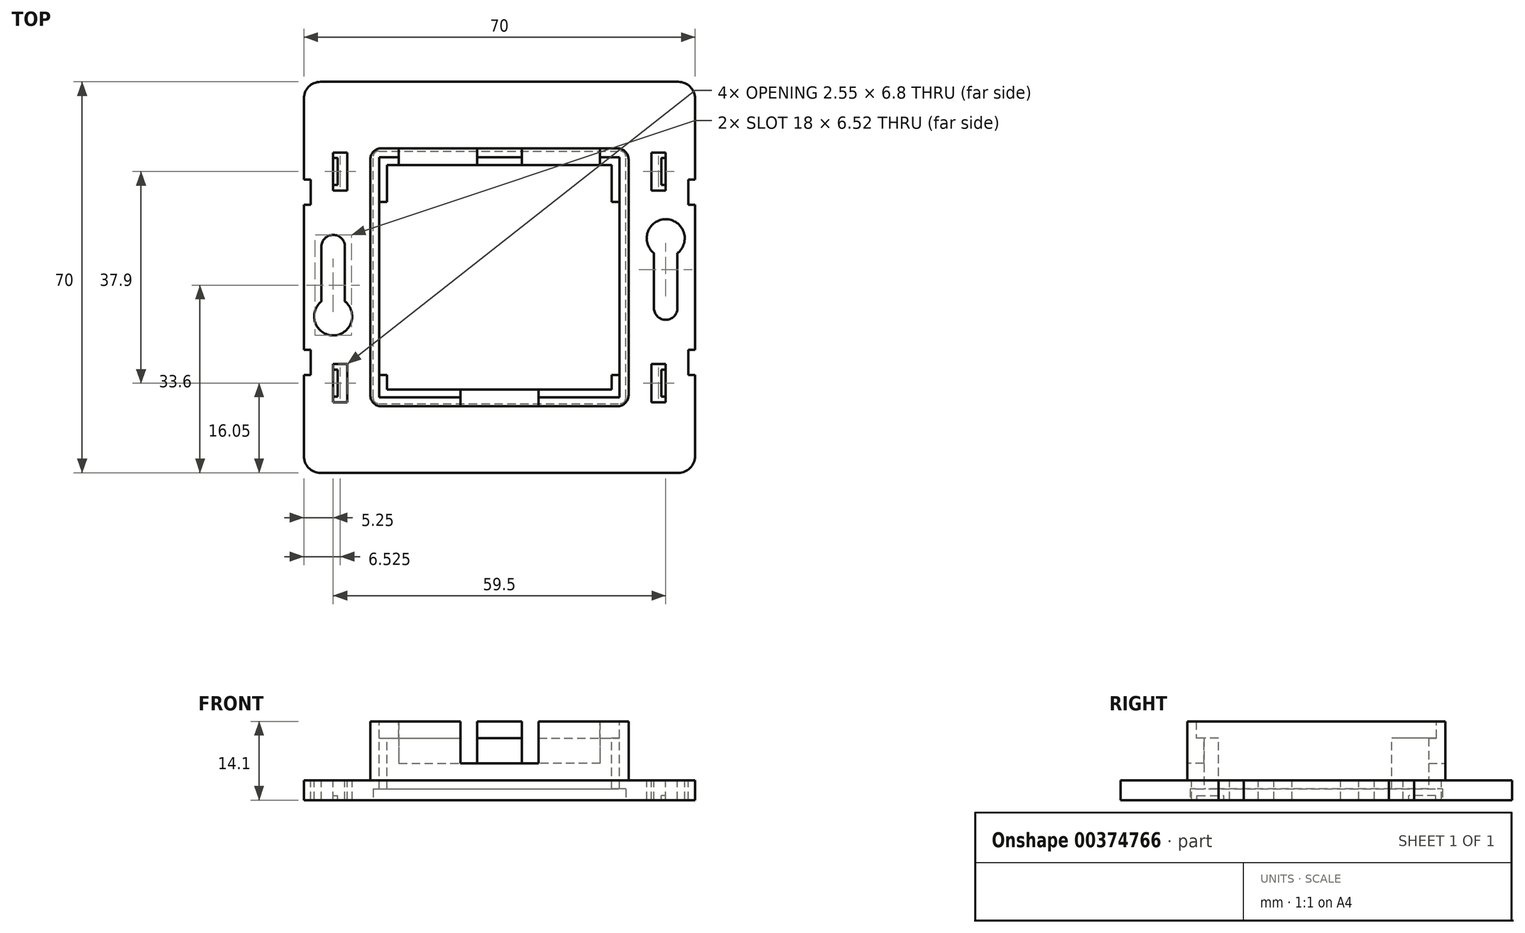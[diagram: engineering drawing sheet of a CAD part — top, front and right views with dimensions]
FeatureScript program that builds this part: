
annotation { "Feature Type Name" : "Feature", "Feature Type Description" : "" }
export const myFeature = defineFeature(function(context is Context, id is Id, definition is map)
    precondition{}
    {
        {
            var Q0;
            Q0=qCreatedBy(makeId("Top.planeOp"),FACE);
            var sketch = newSketch(context, id + "F0", { "sketchPlane" : qUnion([Q0])});
            skLineSegment(sketch, "E0.bottom", {"start": v(-32, 35) * mm, "end": v(32, 35) * mm});
            skLineSegment(sketch, "E0.top", {"start": v(-32, -35) * mm, "end": v(32, -35) * mm});
            skLineSegment(sketch, "E0.left", {"start": v(-35, 32) * mm, "end": v(-35, -32) * mm});
            skLineSegment(sketch, "E0.right", {"start": v(35, 32) * mm, "end": v(35, -32) * mm});
            skPoint(sketch, "E1.visualSharp", {"position": v(-35, 35) * mm});
            skArc(sketch, "E1.filletArc", {"start": v(-32, 35) * mm, "mid": v(-34.12, 34.12) * mm, "end": v(-35, 32) * mm});
            skPoint(sketch, "E2.visualSharp", {"position": v(35, 35) * mm});
            skArc(sketch, "E2.filletArc", {"start": v(35, 32) * mm, "mid": v(34.12, 34.12) * mm, "end": v(32, 35) * mm});
            skPoint(sketch, "E3.visualSharp", {"position": v(35, -35) * mm});
            skArc(sketch, "E3.filletArc", {"start": v(32, -35) * mm, "mid": v(34.12, -34.12) * mm, "end": v(35, -32) * mm});
            skPoint(sketch, "E4.visualSharp", {"position": v(-35, -35) * mm});
            skArc(sketch, "E4.filletArc", {"start": v(-35, -32) * mm, "mid": v(-34.12, -34.12) * mm, "end": v(-32, -35) * mm});
            skLineSegment(sketch, "E5.bottom", {"start": v(-20.1, 20.1) * mm, "end": v(20.1, 20.1) * mm});
            skLineSegment(sketch, "E5.top", {"start": v(-20.1, -20.1) * mm, "end": v(20.1, -20.1) * mm});
            skLineSegment(sketch, "E5.left", {"start": v(-20.1, 20.1) * mm, "end": v(-20.1, -20.1) * mm});
            skLineSegment(sketch, "E5.right", {"start": v(20.1, 20.1) * mm, "end": v(20.1, -20.1) * mm});
            skLineSegment(sketch, "E6.0", {"start": v(23.1, 21.1) * mm, "end": v(23.1, -21.1) * mm});
            skLineSegment(sketch, "E6.1", {"start": v(-21.1, 23.1) * mm, "end": v(21.1, 23.1) * mm});
            skLineSegment(sketch, "E6.2", {"start": v(-23.1, 21.1) * mm, "end": v(-23.1, -21.1) * mm});
            skLineSegment(sketch, "E6.3", {"start": v(-21.1, -23.1) * mm, "end": v(21.1, -23.1) * mm});
            skPoint(sketch, "E7.visualSharp", {"position": v(-23.1, 23.1) * mm});
            skArc(sketch, "E7.filletArc", {"start": v(-21.1, 23.1) * mm, "mid": v(-22.51, 22.51) * mm, "end": v(-23.1, 21.1) * mm});
            skPoint(sketch, "E8.visualSharp", {"position": v(23.1, 23.1) * mm});
            skArc(sketch, "E8.filletArc", {"start": v(23.1, 21.1) * mm, "mid": v(22.51, 22.51) * mm, "end": v(21.1, 23.1) * mm});
            skPoint(sketch, "E9.visualSharp", {"position": v(23.1, -23.1) * mm});
            skArc(sketch, "E9.filletArc", {"start": v(21.1, -23.1) * mm, "mid": v(22.51, -22.51) * mm, "end": v(23.1, -21.1) * mm});
            skPoint(sketch, "E10.visualSharp", {"position": v(-23.1, -23.1) * mm});
            skArc(sketch, "E10.filletArc", {"start": v(-23.1, -21.1) * mm, "mid": v(-22.51, -22.51) * mm, "end": v(-21.1, -23.1) * mm});
            skSolve(sketch);
        }
        {
            var Q0;
            Q0=makeQuery(id+"F0.imprint","IMPRINT",FACE,{"disambiguationData":[TD([[makeQuery(id+"F0.imprint","IMPRINT",EDGE,{"derivedFrom":sQuery(id+"F0.wireOp",EDGE,"E5.bottom")}),1.0]])]});
            extrude(context, id + "F1", {"entities" : qUnion([Q0]), "depth" : 14.1 * mm});
        }
        {
            var Q0;
            Q0=makeQuery(id+"F0.imprint","IMPRINT",FACE,{"disambiguationData":[TD([[makeQuery(id+"F0.imprint","IMPRINT",EDGE,{"derivedFrom":sQuery(id+"F0.wireOp",EDGE,"E0.bottom")}),-1.0]])]});
            extrude(context, id + "F2", {"entities" : qUnion([Q0]), "operationType" : NewBodyOperationType.ADD, "depth" : 3.5 * mm});
        }
        {
            var Q0;
            Q0=makeQuery(id+"F2.opExtrude","CAP_FACE",FACE,{"disambiguationData":[OSD([sQuery(id+"F0.wireOp",EDGE,"E0.bottom"),sQuery(id+"F0.wireOp",EDGE,"E0.top"),sQuery(id+"F0.wireOp",EDGE,"E0.left"),sQuery(id+"F0.wireOp",EDGE,"E0.right"),sQuery(id+"F0.wireOp",EDGE,"8215a4ff-56be-4c60-a47c-f66ea536b4aa.0"),sQuery(id+"F0.wireOp",EDGE,"8215a4ff-56be-4c60-a47c-f66ea536b4aa.1"),sQuery(id+"F0.wireOp",EDGE,"8215a4ff-56be-4c60-a47c-f66ea536b4aa.2"),sQuery(id+"F0.wireOp",EDGE,"8215a4ff-56be-4c60-a47c-f66ea536b4aa.3"),sQuery(id+"F0.wireOp",EDGE,"E1.filletArc"),sQuery(id+"F0.wireOp",EDGE,"E2.filletArc"),sQuery(id+"F0.wireOp",EDGE,"E3.filletArc"),sQuery(id+"F0.wireOp",EDGE,"E4.filletArc"),sQuery(id+"F0.wireOp",EDGE,"55755b73-03b5-497c-a17b-18f3f700d980.filletArc"),sQuery(id+"F0.wireOp",EDGE,"18d8bc87-035d-4be4-8c5c-5c0431c61aee.filletArc"),sQuery(id+"F0.wireOp",EDGE,"c21042aa-8350-4172-84ff-4aa2e3af1f04.filletArc"),sQuery(id+"F0.wireOp",EDGE,"eb6bf6a7-3b97-4e9c-9c9c-5d018f2c8f51.filletArc")])],"isStart":false});
            var sketch = newSketch(context, id + "F3", { "sketchPlane" : qUnion([Q0])});
            skLineSegment(sketch, "E11.bottom", {"start": v(-35, 13) * mm, "end": v(-33.8, 13) * mm});
            skLineSegment(sketch, "E11.top", {"start": v(-35, 17.5) * mm, "end": v(-33.8, 17.5) * mm});
            skLineSegment(sketch, "E11.left", {"start": v(-35, 17.5) * mm, "end": v(-35, 13) * mm});
            skLineSegment(sketch, "E11.right", {"start": v(-33.8, 17.5) * mm, "end": v(-33.8, 13) * mm});
            skLineSegment(sketch, "E12.bottom", {"start": v(35, -17.5) * mm, "end": v(33.8, -17.5) * mm});
            skLineSegment(sketch, "E12.top", {"start": v(35, -13) * mm, "end": v(33.8, -13) * mm});
            skLineSegment(sketch, "E12.left", {"start": v(35, -17.5) * mm, "end": v(35, -13) * mm});
            skLineSegment(sketch, "E12.right", {"start": v(33.8, -17.5) * mm, "end": v(33.8, -13) * mm});
            skArc(sketch, "E13", {"start": v(31.85, 4.33) * mm, "mid": v(29.75, 10.4) * mm, "end": v(27.65, 4.33) * mm});
            skArc(sketch, "E14", {"start": v(27.65, -5.5) * mm, "mid": v(29.75, -7.6) * mm, "end": v(31.85, -5.5) * mm});
            skLineSegment(sketch, "E15", {"start": v(27.65, -5.5) * mm, "end": v(27.65, 4.33) * mm});
            skLineSegment(sketch, "E16", {"start": v(31.85, -5.5) * mm, "end": v(31.85, 4.33) * mm});
            skArc(sketch, "E17.MirrorC", {"start": v(-31.85, 5.5) * mm, "mid": v(-29.75, 7.6) * mm, "end": v(-27.65, 5.5) * mm});
            skLineSegment(sketch, "E18.MirrorCS", {"start": v(-27.65, 5.5) * mm, "end": v(-27.65, -4.33) * mm});
            skLineSegment(sketch, "E19.MirrorCS", {"start": v(-31.85, 5.5) * mm, "end": v(-31.85, -4.33) * mm});
            skArc(sketch, "E20.MirrorC", {"start": v(-27.65, -4.33) * mm, "mid": v(-29.75, -10.4) * mm, "end": v(-31.85, -4.33) * mm});
            skLineSegment(sketch, "E21.MirrorCS", {"start": v(33.8, 17.5) * mm, "end": v(33.8, 13) * mm});
            skLineSegment(sketch, "E22.MirrorCS", {"start": v(35, 17.5) * mm, "end": v(35, 13) * mm});
            skLineSegment(sketch, "E23.MirrorCS", {"start": v(35, 17.5) * mm, "end": v(33.8, 17.5) * mm});
            skLineSegment(sketch, "E24.MirrorCS", {"start": v(35, 13) * mm, "end": v(33.8, 13) * mm});
            skLineSegment(sketch, "E25.MirrorCS", {"start": v(-35, -17.5) * mm, "end": v(-35, -13) * mm});
            skLineSegment(sketch, "E26.MirrorCS", {"start": v(-33.8, -17.5) * mm, "end": v(-33.8, -13) * mm});
            skLineSegment(sketch, "E27.MirrorCS", {"start": v(-35, -13) * mm, "end": v(-33.8, -13) * mm});
            skLineSegment(sketch, "E28.MirrorCS", {"start": v(-35, -17.5) * mm, "end": v(-33.8, -17.5) * mm});
            skSolve(sketch);
        }
        {
            var Q0;
            Q0 = qSketchRegion(id + "F3", true);
            extrude(context, id + "F4", {"entities" : qUnion([Q0]), "operationType" : NewBodyOperationType.REMOVE, "oppositeDirection" : true, "depth" : 25 * mm});
        }
        {
            var Q0;
            Q0=qCreatedBy(makeId("Top.planeOp"),FACE);
            var sketch = newSketch(context, id + "F5", { "sketchPlane" : qUnion([Q0])});
            skLineSegment(sketch, "E29.bottom", {"start": v(-21.6, -22.6) * mm, "end": v(21.6, -22.6) * mm});
            skLineSegment(sketch, "E29.top", {"start": v(-21.6, 22.6) * mm, "end": v(21.6, 22.6) * mm});
            skLineSegment(sketch, "E29.left", {"start": v(-22.6, -21.6) * mm, "end": v(-22.6, 21.6) * mm});
            skLineSegment(sketch, "E29.right", {"start": v(22.6, -21.6) * mm, "end": v(22.6, 21.6) * mm});
            skPoint(sketch, "E30.visualSharp", {"position": v(-22.6, -22.6) * mm});
            skArc(sketch, "E30.filletArc", {"start": v(-22.6, -21.6) * mm, "mid": v(-22.3, -22.3) * mm, "end": v(-21.6, -22.6) * mm});
            skPoint(sketch, "E31.visualSharp", {"position": v(22.6, -22.6) * mm});
            skArc(sketch, "E31.filletArc", {"start": v(21.6, -22.6) * mm, "mid": v(22.3, -22.3) * mm, "end": v(22.6, -21.6) * mm});
            skPoint(sketch, "E32.visualSharp", {"position": v(22.6, 22.6) * mm});
            skArc(sketch, "E32.filletArc", {"start": v(22.6, 21.6) * mm, "mid": v(22.3, 22.3) * mm, "end": v(21.6, 22.6) * mm});
            skPoint(sketch, "E33.visualSharp", {"position": v(-22.6, 22.6) * mm});
            skArc(sketch, "E33.filletArc", {"start": v(-21.6, 22.6) * mm, "mid": v(-22.3, 22.3) * mm, "end": v(-22.6, 21.6) * mm});
            skSolve(sketch);
        }
        {
            var Q0;
            Q0 = qSketchRegion(id + "F5", true);
            extrude(context, id + "F6", {"entities" : qUnion([Q0]), "operationType" : NewBodyOperationType.REMOVE, "depth" : 2 * mm});
        }
        {
            var Q0;
            Q0=makeQuery(id+"F1.opExtrude","CAP_FACE",FACE,{"disambiguationData":[OSD([sQuery(id+"F0.wireOp",EDGE,"E5.bottom"),sQuery(id+"F0.wireOp",EDGE,"E5.top"),sQuery(id+"F0.wireOp",EDGE,"E5.left"),sQuery(id+"F0.wireOp",EDGE,"E5.right"),sQuery(id+"F0.wireOp",EDGE,"E6.0"),sQuery(id+"F0.wireOp",EDGE,"E6.1"),sQuery(id+"F0.wireOp",EDGE,"E6.2"),sQuery(id+"F0.wireOp",EDGE,"E6.3"),sQuery(id+"F0.wireOp",EDGE,"E7.filletArc"),sQuery(id+"F0.wireOp",EDGE,"E8.filletArc"),sQuery(id+"F0.wireOp",EDGE,"E9.filletArc"),sQuery(id+"F0.wireOp",EDGE,"E10.filletArc")])],"isStart":false});
            var sketch = newSketch(context, id + "F7", { "sketchPlane" : qUnion([Q0])});
            skLineSegment(sketch, "E34.bottom", {"start": v(-20.1, 20.1) * mm, "end": v(20.1, 20.1) * mm});
            skLineSegment(sketch, "E34.top", {"start": v(-20.1, -20.1) * mm, "end": v(20.1, -20.1) * mm});
            skLineSegment(sketch, "E34.left", {"start": v(-20.1, 20.1) * mm, "end": v(-20.1, -20.1) * mm});
            skLineSegment(sketch, "E34.right", {"start": v(20.1, 20.1) * mm, "end": v(20.1, -20.1) * mm});
            skLineSegment(sketch, "E35.0", {"start": v(-21.5, -21.5) * mm, "end": v(21.5, -21.5) * mm});
            skLineSegment(sketch, "E35.1", {"start": v(-21.5, 21.5) * mm, "end": v(-21.5, -21.5) * mm});
            skLineSegment(sketch, "E35.2", {"start": v(-21.5, 21.5) * mm, "end": v(21.5, 21.5) * mm});
            skLineSegment(sketch, "E35.3", {"start": v(21.5, 21.5) * mm, "end": v(21.5, -21.5) * mm});
            skSolve(sketch);
        }
        {
            var Q0;
            Q0=makeQuery(id+"F7.imprint","IMPRINT",FACE,{"disambiguationData":[TD([[makeQuery(id+"F7.imprint","IMPRINT",EDGE,{"derivedFrom":sQuery(id+"F7.wireOp",EDGE,"E34.bottom")}),1.0]])]});
            extrude(context, id + "F8", {"entities" : qUnion([Q0]), "operationType" : NewBodyOperationType.REMOVE, "oppositeDirection" : true, "depth" : 3 * mm});
        }
        {
            var Q0;
            Q0=makeQuery(id+"F1.opExtrude","SWEPT_FACE",FACE,{"disambiguationData":[OSD([sQuery(id+"F0.wireOp",EDGE,"E6.3")])]});
            var sketch = newSketch(context, id + "F9", { "sketchPlane" : qUnion([Q0])});
            skLineSegment(sketch, "E36.bottom", {"start": v(-7, 14.1) * mm, "end": v(7, 14.1) * mm});
            skLineSegment(sketch, "E36.top", {"start": v(-7, 6.6) * mm, "end": v(7, 6.6) * mm});
            skLineSegment(sketch, "E36.left", {"start": v(-7, 14.1) * mm, "end": v(-7, 6.6) * mm});
            skLineSegment(sketch, "E36.right", {"start": v(7, 14.1) * mm, "end": v(7, 6.6) * mm});
            skSolve(sketch);
        }
        {
            var Q0;
            Q0=makeQuery(id+"F9.imprint","IMPRINT",FACE,{"disambiguationData":[TD([[makeQuery(id+"F9.imprint","IMPRINT",EDGE,{"derivedFrom":sQuery(id+"F9.wireOp",EDGE,"E36.bottom")}),-1.0]])]});
            extrude(context, id + "F10", {"entities" : qUnion([Q0]), "operationType" : NewBodyOperationType.REMOVE, "oppositeDirection" : true, "depth" : 5 * mm});
        }
        {
            var Q0;
            Q0=makeQuery(id+"F1.opExtrude","SWEPT_FACE",FACE,{"disambiguationData":[OSD([sQuery(id+"F0.wireOp",EDGE,"E6.1")])]});
            var sketch = newSketch(context, id + "F11", { "sketchPlane" : qUnion([Q0])});
            skLineSegment(sketch, "E37.bottom", {"start": v(-18, 14.1) * mm, "end": v(-4, 14.1) * mm});
            skLineSegment(sketch, "E37.top", {"start": v(-18, 6.6) * mm, "end": v(-4, 6.6) * mm});
            skLineSegment(sketch, "E37.left", {"start": v(-18, 14.1) * mm, "end": v(-18, 6.6) * mm});
            skLineSegment(sketch, "E37.right", {"start": v(-4, 14.1) * mm, "end": v(-4, 6.6) * mm});
            skLineSegment(sketch, "E38.MirrorCS", {"start": v(18, 6.6) * mm, "end": v(4, 6.6) * mm});
            skLineSegment(sketch, "E39.MirrorCS", {"start": v(4, 14.1) * mm, "end": v(4, 6.6) * mm});
            skLineSegment(sketch, "E40.MirrorCS", {"start": v(18, 14.1) * mm, "end": v(18, 6.6) * mm});
            skLineSegment(sketch, "E41.MirrorCS", {"start": v(18, 14.1) * mm, "end": v(4, 14.1) * mm});
            skSolve(sketch);
        }
        {
            var Q0;
            Q0=makeQuery(id+"F11.imprint","IMPRINT",FACE,{"disambiguationData":[TD([[makeQuery(id+"F11.imprint","IMPRINT",EDGE,{"derivedFrom":sQuery(id+"F11.wireOp",EDGE,"E37.bottom")}),1.0]])]});
            var Q1;
            Q1=makeQuery(id+"F11.imprint","IMPRINT",FACE,{"disambiguationData":[TD([[makeQuery(id+"F11.imprint","IMPRINT",EDGE,{"derivedFrom":sQuery(id+"F11.wireOp",EDGE,"E38.MirrorCS")}),-1.0]])]});
            extrude(context, id + "F12", {"entities" : qUnion([Q0, Q1]), "operationType" : NewBodyOperationType.REMOVE, "oppositeDirection" : true, "depth" : 5 * mm});
        }
        {
            var Q0;
            {var subQ0=sQuery(id+"F7.wireOp",EDGE,"E35.2");var subQ1=sQuery(id+"F7.wireOp",EDGE,"E35.1");var subQ2=sQuery(id+"F7.wireOp",EDGE,"E35.0");Q0=makeQuery(id+"F12.boolean.opBoolean","SPLIT",FACE,{"disambiguationData":[TD([makeQuery(id+"F1.opExtrude","SWEPT_FACE",FACE,{"disambiguationData":[OSD([sQuery(id+"F0.wireOp",EDGE,"E5.left")])]})])],"derivedFrom":makeQuery(id+"F8.boolean.opBoolean","COPY",FACE,{"derivedFrom":makeQuery(id+"F8.opExtrude","CAP_FACE",FACE,{"disambiguationData":[OSD([sQuery(id+"F7.wireOp",EDGE,"E34.bottom"),sQuery(id+"F7.wireOp",EDGE,"E34.top"),sQuery(id+"F7.wireOp",EDGE,"E34.left"),sQuery(id+"F7.wireOp",EDGE,"E34.right"),subQ2,subQ1,subQ0,sQuery(id+"F7.wireOp",EDGE,"E35.3")])],"isStart":false})})});}
            var sketch = newSketch(context, id + "F13", { "sketchPlane" : qUnion([Q0])});
            skLineSegment(sketch, "E42.bottom", {"start": v(-21.5, 13.5) * mm, "end": v(-20.1, 13.5) * mm});
            skLineSegment(sketch, "E42.top", {"start": v(-21.5, -17.5) * mm, "end": v(-20.1, -17.5) * mm});
            skLineSegment(sketch, "E42.left", {"start": v(-21.5, 13.5) * mm, "end": v(-21.5, -17.5) * mm});
            skLineSegment(sketch, "E42.right", {"start": v(-20.1, 13.5) * mm, "end": v(-20.1, -17.5) * mm});
            skLineSegment(sketch, "E43.MirrorCS", {"start": v(21.5, 13.5) * mm, "end": v(20.1, 13.5) * mm});
            skLineSegment(sketch, "E44.MirrorCS", {"start": v(21.5, -17.5) * mm, "end": v(20.1, -17.5) * mm});
            skLineSegment(sketch, "E45.MirrorCS", {"start": v(20.1, 13.5) * mm, "end": v(20.1, -17.5) * mm});
            skLineSegment(sketch, "E46.MirrorCS", {"start": v(21.5, 13.5) * mm, "end": v(21.5, -17.5) * mm});
            skSolve(sketch);
        }
        {
            var Q0;
            Q0=makeQuery(id+"F13.imprint","IMPRINT",FACE,{"disambiguationData":[TD([[makeQuery(id+"F13.imprint","IMPRINT",EDGE,{"derivedFrom":sQuery(id+"F13.wireOp",EDGE,"E42.bottom")}),-1.0]])]});
            var Q1;
            Q1=makeQuery(id+"F13.imprint","IMPRINT",FACE,{"disambiguationData":[TD([[makeQuery(id+"F13.imprint","IMPRINT",EDGE,{"derivedFrom":sQuery(id+"F13.wireOp",EDGE,"E43.MirrorCS")}),1.0]])]});
            extrude(context, id + "F14", {"entities" : qUnion([Q0, Q1]), "operationType" : NewBodyOperationType.REMOVE, "oppositeDirection" : true, "depth" : 15 * mm});
        }
        {
            var Q0;
            Q0=makeQuery(id+"F2.opExtrude","CAP_FACE",FACE,{"disambiguationData":[OSD([sQuery(id+"F0.wireOp",EDGE,"E0.bottom"),sQuery(id+"F0.wireOp",EDGE,"E0.top"),sQuery(id+"F0.wireOp",EDGE,"E0.left"),sQuery(id+"F0.wireOp",EDGE,"E0.right"),sQuery(id+"F0.wireOp",EDGE,"E1.filletArc"),sQuery(id+"F0.wireOp",EDGE,"E2.filletArc"),sQuery(id+"F0.wireOp",EDGE,"E3.filletArc"),sQuery(id+"F0.wireOp",EDGE,"E4.filletArc"),sQuery(id+"F0.wireOp",EDGE,"E6.0"),sQuery(id+"F0.wireOp",EDGE,"E6.1"),sQuery(id+"F0.wireOp",EDGE,"E6.2"),sQuery(id+"F0.wireOp",EDGE,"E6.3"),sQuery(id+"F0.wireOp",EDGE,"E7.filletArc"),sQuery(id+"F0.wireOp",EDGE,"E8.filletArc"),sQuery(id+"F0.wireOp",EDGE,"E9.filletArc"),sQuery(id+"F0.wireOp",EDGE,"E10.filletArc")])],"isStart":false});
            var sketch = newSketch(context, id + "F15", { "sketchPlane" : qUnion([Q0])});
            skLineSegment(sketch, "E47.bottom", {"start": v(-27.2, 22.35) * mm, "end": v(27.2, 22.35) * mm});
            skLineSegment(sketch, "E47.top", {"start": v(-27.2, -22.35) * mm, "end": v(27.2, -22.35) * mm});
            skLineSegment(sketch, "E47.left", {"start": v(-27.2, 22.35) * mm, "end": v(-27.2, -22.35) * mm});
            skLineSegment(sketch, "E47.right", {"start": v(27.2, 22.35) * mm, "end": v(27.2, -22.35) * mm});
            skLineSegment(sketch, "E48.bottom", {"start": v(-27.2, 22.35) * mm, "end": v(-29.75, 22.35) * mm});
            skLineSegment(sketch, "E48.top", {"start": v(-27.2, 15.55) * mm, "end": v(-29.75, 15.55) * mm});
            skLineSegment(sketch, "E48.left", {"start": v(-27.2, 22.35) * mm, "end": v(-27.2, 15.55) * mm});
            skLineSegment(sketch, "E48.right", {"start": v(-29.75, 22.35) * mm, "end": v(-29.75, 21.35) * mm});
            skLineSegment(sketch, "E49.bottom", {"start": v(-29.75, 21.35) * mm, "end": v(-28.95, 21.35) * mm});
            skLineSegment(sketch, "E49.top", {"start": v(-29.75, 16.55) * mm, "end": v(-28.95, 16.55) * mm});
            skLineSegment(sketch, "E49.right", {"start": v(-28.95, 21.35) * mm, "end": v(-28.95, 16.55) * mm});
            skLineSegment(sketch, "E50.trimOffspring", {"start": v(-29.75, 16.55) * mm, "end": v(-29.75, 15.55) * mm});
            skLineSegment(sketch, "E51.MirrorCS", {"start": v(-29.75, -21.35) * mm, "end": v(-28.95, -21.35) * mm});
            skLineSegment(sketch, "E52.MirrorCS", {"start": v(-29.75, -22.35) * mm, "end": v(-29.75, -21.35) * mm});
            skLineSegment(sketch, "E53.MirrorCS", {"start": v(-29.75, -16.55) * mm, "end": v(-28.95, -16.55) * mm});
            skLineSegment(sketch, "E54.MirrorCS", {"start": v(-29.75, -16.55) * mm, "end": v(-29.75, -15.55) * mm});
            skLineSegment(sketch, "E55.MirrorCS", {"start": v(-27.2, -22.35) * mm, "end": v(-27.2, -15.55) * mm});
            skLineSegment(sketch, "E56.MirrorCS", {"start": v(-27.2, -15.55) * mm, "end": v(-29.75, -15.55) * mm});
            skLineSegment(sketch, "E57.MirrorCS", {"start": v(-28.95, -21.35) * mm, "end": v(-28.95, -16.55) * mm});
            skLineSegment(sketch, "E58.MirrorCS", {"start": v(-27.2, -22.35) * mm, "end": v(-29.75, -22.35) * mm});
            skLineSegment(sketch, "E59.MirrorCS", {"start": v(-27.2, -22.35) * mm, "end": v(-27.2, 22.35) * mm});
            skLineSegment(sketch, "E60.MirrorCS", {"start": v(27.2, -22.35) * mm, "end": v(29.75, -22.35) * mm});
            skLineSegment(sketch, "E61.MirrorCS", {"start": v(27.2, -22.35) * mm, "end": v(27.2, -15.55) * mm});
            skLineSegment(sketch, "E62.MirrorCS", {"start": v(29.75, -16.55) * mm, "end": v(28.95, -16.55) * mm});
            skLineSegment(sketch, "E63.MirrorCS", {"start": v(29.75, -16.55) * mm, "end": v(29.75, -15.55) * mm});
            skLineSegment(sketch, "E64.MirrorCS", {"start": v(28.95, -21.35) * mm, "end": v(28.95, -16.55) * mm});
            skLineSegment(sketch, "E65.MirrorCS", {"start": v(29.75, -21.35) * mm, "end": v(28.95, -21.35) * mm});
            skLineSegment(sketch, "E66.MirrorCS", {"start": v(27.2, -15.55) * mm, "end": v(29.75, -15.55) * mm});
            skLineSegment(sketch, "E67.MirrorCS", {"start": v(29.75, -22.35) * mm, "end": v(29.75, -21.35) * mm});
            skLineSegment(sketch, "E68.MirrorCS", {"start": v(29.75, 21.35) * mm, "end": v(28.95, 21.35) * mm});
            skLineSegment(sketch, "E69.MirrorCS", {"start": v(29.75, 16.55) * mm, "end": v(29.75, 15.55) * mm});
            skLineSegment(sketch, "E70.MirrorCS", {"start": v(29.75, 22.35) * mm, "end": v(29.75, 21.35) * mm});
            skLineSegment(sketch, "E71.MirrorCS", {"start": v(29.75, 16.55) * mm, "end": v(28.95, 16.55) * mm});
            skLineSegment(sketch, "E72.MirrorCS", {"start": v(27.2, 22.35) * mm, "end": v(29.75, 22.35) * mm});
            skLineSegment(sketch, "E73.MirrorCS", {"start": v(28.95, 21.35) * mm, "end": v(28.95, 16.55) * mm});
            skLineSegment(sketch, "E74.MirrorCS", {"start": v(27.2, 22.35) * mm, "end": v(27.2, 15.55) * mm});
            skLineSegment(sketch, "E75.MirrorCS", {"start": v(27.2, 15.55) * mm, "end": v(29.75, 15.55) * mm});
            skLineSegment(sketch, "E76", {"start": v(-29.75, 21.35) * mm, "end": v(-29.75, 16.55) * mm});
            skLineSegment(sketch, "E77", {"start": v(29.75, 21.35) * mm, "end": v(29.75, 16.55) * mm});
            skLineSegment(sketch, "E78", {"start": v(-29.75, -16.55) * mm, "end": v(-29.75, -21.35) * mm});
            skLineSegment(sketch, "E79", {"start": v(29.75, -16.55) * mm, "end": v(29.75, -21.35) * mm});
            skSolve(sketch);
        }
        {
            var Q0;
            Q0=makeQuery(id+"F15.imprint","IMPRINT",FACE,{"disambiguationData":[TD([[makeQuery(id+"F15.imprint","IMPRINT",EDGE,{"derivedFrom":sQuery(id+"F15.wireOp",EDGE,"E49.bottom")}),1.0]])]});
            var Q1;
            Q1=makeQuery(id+"F15.imprint","IMPRINT",FACE,{"disambiguationData":[TD([[makeQuery(id+"F15.imprint","IMPRINT",EDGE,{"derivedFrom":sQuery(id+"F15.wireOp",EDGE,"E49.bottom")}),-1.0]])]});
            var Q2;
            Q2=makeQuery(id+"F15.imprint","IMPRINT",FACE,{"disambiguationData":[TD([[makeQuery(id+"F15.imprint","IMPRINT",EDGE,{"derivedFrom":sQuery(id+"F15.wireOp",EDGE,"E71.MirrorCS")}),-1.0]])]});
            var Q3;
            Q3=makeQuery(id+"F15.imprint","IMPRINT",FACE,{"disambiguationData":[TD([[makeQuery(id+"F15.imprint","IMPRINT",EDGE,{"derivedFrom":sQuery(id+"F15.wireOp",EDGE,"E71.MirrorCS")}),1.0]])]});
            var Q4;
            Q4=makeQuery(id+"F15.imprint","IMPRINT",FACE,{"disambiguationData":[TD([[makeQuery(id+"F15.imprint","IMPRINT",EDGE,{"derivedFrom":sQuery(id+"F15.wireOp",EDGE,"E64.MirrorCS")}),1.0]])]});
            var Q5;
            Q5=makeQuery(id+"F15.imprint","IMPRINT",FACE,{"disambiguationData":[TD([[makeQuery(id+"F15.imprint","IMPRINT",EDGE,{"derivedFrom":sQuery(id+"F15.wireOp",EDGE,"E64.MirrorCS")}),-1.0]])]});
            var Q6;
            Q6=makeQuery(id+"F15.imprint","IMPRINT",FACE,{"disambiguationData":[TD([[makeQuery(id+"F15.imprint","IMPRINT",EDGE,{"derivedFrom":sQuery(id+"F15.wireOp",EDGE,"E54.MirrorCS")}),-1.0]])]});
            var Q7;
            Q7=makeQuery(id+"F15.imprint","IMPRINT",FACE,{"disambiguationData":[TD([[makeQuery(id+"F15.imprint","IMPRINT",EDGE,{"derivedFrom":sQuery(id+"F15.wireOp",EDGE,"E51.MirrorCS")}),1.0]])]});
            extrude(context, id + "F16", {"entities" : qUnion([Q0, Q1, Q2, Q3, Q4, Q5, Q6, Q7]), "operationType" : NewBodyOperationType.REMOVE, "oppositeDirection" : true, "depth" : 2.7 * mm});
        }
        {
            var Q0;
            Q0=makeQuery(id+"F15.imprint","IMPRINT",FACE,{"disambiguationData":[TD([[makeQuery(id+"F15.imprint","IMPRINT",EDGE,{"derivedFrom":sQuery(id+"F15.wireOp",EDGE,"E49.bottom")}),1.0]])]});
            var Q1;
            Q1=makeQuery(id+"F15.imprint","IMPRINT",FACE,{"disambiguationData":[TD([[makeQuery(id+"F15.imprint","IMPRINT",EDGE,{"derivedFrom":sQuery(id+"F15.wireOp",EDGE,"E71.MirrorCS")}),1.0]])]});
            var Q2;
            Q2=makeQuery(id+"F15.imprint","IMPRINT",FACE,{"disambiguationData":[TD([[makeQuery(id+"F15.imprint","IMPRINT",EDGE,{"derivedFrom":sQuery(id+"F15.wireOp",EDGE,"E64.MirrorCS")}),1.0]])]});
            var Q3;
            Q3=makeQuery(id+"F15.imprint","IMPRINT",FACE,{"disambiguationData":[TD([[makeQuery(id+"F15.imprint","IMPRINT",EDGE,{"derivedFrom":sQuery(id+"F15.wireOp",EDGE,"E54.MirrorCS")}),-1.0]])]});
            extrude(context, id + "F17", {"entities" : qUnion([Q0, Q1, Q2, Q3]), "operationType" : NewBodyOperationType.REMOVE, "oppositeDirection" : true, "depth" : 7 * mm});
        }
    });
